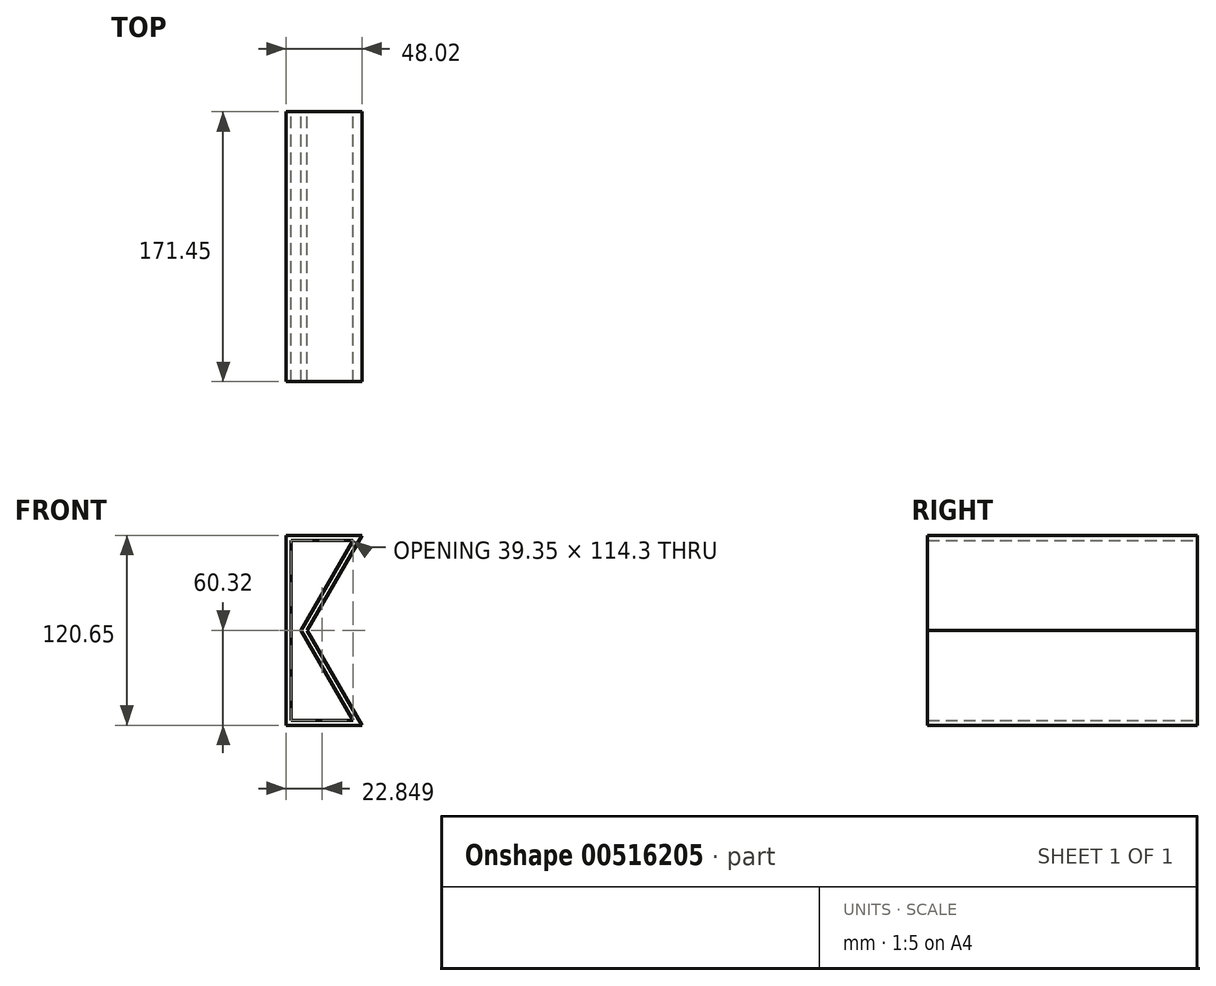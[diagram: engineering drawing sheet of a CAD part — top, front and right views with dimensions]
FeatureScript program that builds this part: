
annotation { "Feature Type Name" : "Feature", "Feature Type Description" : "" }
export const myFeature = defineFeature(function(context is Context, id is Id, definition is map)
    precondition{}
    {
        {
            var Q0;
            Q0=qCreatedBy(makeId("Front.planeOp"),FACE);
            var sketch = newSketch(context, id + "F0", { "sketchPlane" : qUnion([Q0])});
            skCircle(sketch, "E0.cCircle", {"center": v(0, 0) * mm, "radius": 60.33 * mm, "construction": true});
            skLineSegment(sketch, "E0.0", {"start": v(-34.83, 60.33) * mm, "end": v(34.83, 60.33) * mm});
            skLineSegment(sketch, "E0.1", {"start": v(34.83, 60.33) * mm, "end": v(69.66, 0) * mm});
            skLineSegment(sketch, "E0.2", {"start": v(69.66, 0) * mm, "end": v(34.83, -60.32) * mm});
            skLineSegment(sketch, "E0.3", {"start": v(34.83, -60.32) * mm, "end": v(-34.83, -60.33) * mm});
            skLineSegment(sketch, "E0.4", {"start": v(-34.83, -60.33) * mm, "end": v(-69.66, 0) * mm});
            skLineSegment(sketch, "E0.5", {"start": v(-69.66, 0) * mm, "end": v(-34.83, 60.32) * mm});
            skPoint(sketch, "E0.0.midPoint", {"position": v(0, 60.33) * mm});
            skLineSegment(sketch, "E1", {"start": v(-34.83, -60.33) * mm, "end": v(-82.85, -60.33) * mm});
            skLineSegment(sketch, "E2", {"start": v(-82.85, -60.33) * mm, "end": v(-82.85, 60.33) * mm});
            skLineSegment(sketch, "E3", {"start": v(-82.85, 60.33) * mm, "end": v(-34.83, 60.33) * mm});
            skLineSegment(sketch, "E4.0", {"start": v(-79.67, 57.15) * mm, "end": v(-40.33, 57.15) * mm});
            skLineSegment(sketch, "E4.1", {"start": v(-73.32, 0) * mm, "end": v(-40.33, 57.15) * mm});
            skLineSegment(sketch, "E4.2", {"start": v(-79.67, -57.15) * mm, "end": v(-79.67, 57.15) * mm});
            skLineSegment(sketch, "E4.3", {"start": v(-40.33, -57.15) * mm, "end": v(-79.67, -57.15) * mm});
            skLineSegment(sketch, "E4.4", {"start": v(-40.33, -57.15) * mm, "end": v(-73.32, 0) * mm});
            skSolve(sketch);
        }
        {
            var Q0;
            Q0=makeQuery(id+"F0.imprint","IMPRINT",FACE,{"disambiguationData":[TD([[makeQuery(id+"F0.imprint","IMPRINT",EDGE,{"derivedFrom":sQuery(id+"F0.wireOp",EDGE,"E0.4")}),1.0]])]});
            extrude(context, id + "F1", {"entities" : qUnion([Q0]), "depth" : 171.45 * mm, "offsetDistance" : 25.4 * mm});
        }
    });
